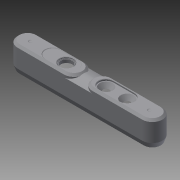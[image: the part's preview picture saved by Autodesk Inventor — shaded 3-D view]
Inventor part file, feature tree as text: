
AUTODESK INVENTOR PART (.ipt)
format: ipt  version: 2013 (Build 170138000, 138)  size: 322,560 bytes
history: native  units: mm
features: chamfer x10, extrude x7, sketch x7, fillet x5, other x3
ambient origin geometry x8: Origin, YZ Plane, XZ Plane, XY Plane, X Axis, Y Axis, Z Axis, Center Point
feature tree (32):
  other  "ソリッド1"
  extrude  "押し出し1"  Depth=25.0mm
  chamfer  "面取り1"  Distance=12.5mm
  extrude  "押し出し6"  Depth=25.0mm
  chamfer  "面取り7"  Distance=154.0mm
  chamfer  "面取り9"  Distance=79.0mm
  fillet  "フィレット4"  Radius=29.5mm
  chamfer  "面取り11"  Distance=2.0mm Angle=45.0deg
  fillet  "フィレット5"  Radius=57.5mm
  fillet  "フィレット6"  Radius=61.5mm
  chamfer  "面取り12"  Distance=12.5mm
  extrude  "押し出し7"  Depth=12.5mm
  extrude  "押し出し8"  Depth=1.5mm TaperAngle=0.0deg
  chamfer  "面取り13"  Distance=1.5mm Angle=45.0deg
  fillet  "フィレット7"  Radius=1.5mm
  chamfer  "面取り14"  Distance=15.0mm
  extrude  "押し出し9"  Depth=2.5mm TaperAngle=30.0deg
  chamfer  "面取り15"  Distance=40.0mm
  chamfer  "面取り16"  Distance=12.0mm
  extrude  "押し出し10"  Depth=2.5mm TaperAngle=30.0deg
  extrude  "押し出し11"  Depth=19.0mm
  chamfer  "面取り17"  Distance=10.0mm
  fillet  "フィレット8"  Radius=10.0mm
  sketch  "スケッチ1"
  sketch  "スケッチ7"
  sketch  "スケッチ8"
  sketch  "スケッチ10"
  sketch  "スケッチ11"
  sketch  "スケッチ12"
  sketch  "スケッチ13"
  other  "断面エッジを投影1"
  other  "断面エッジを投影2"
